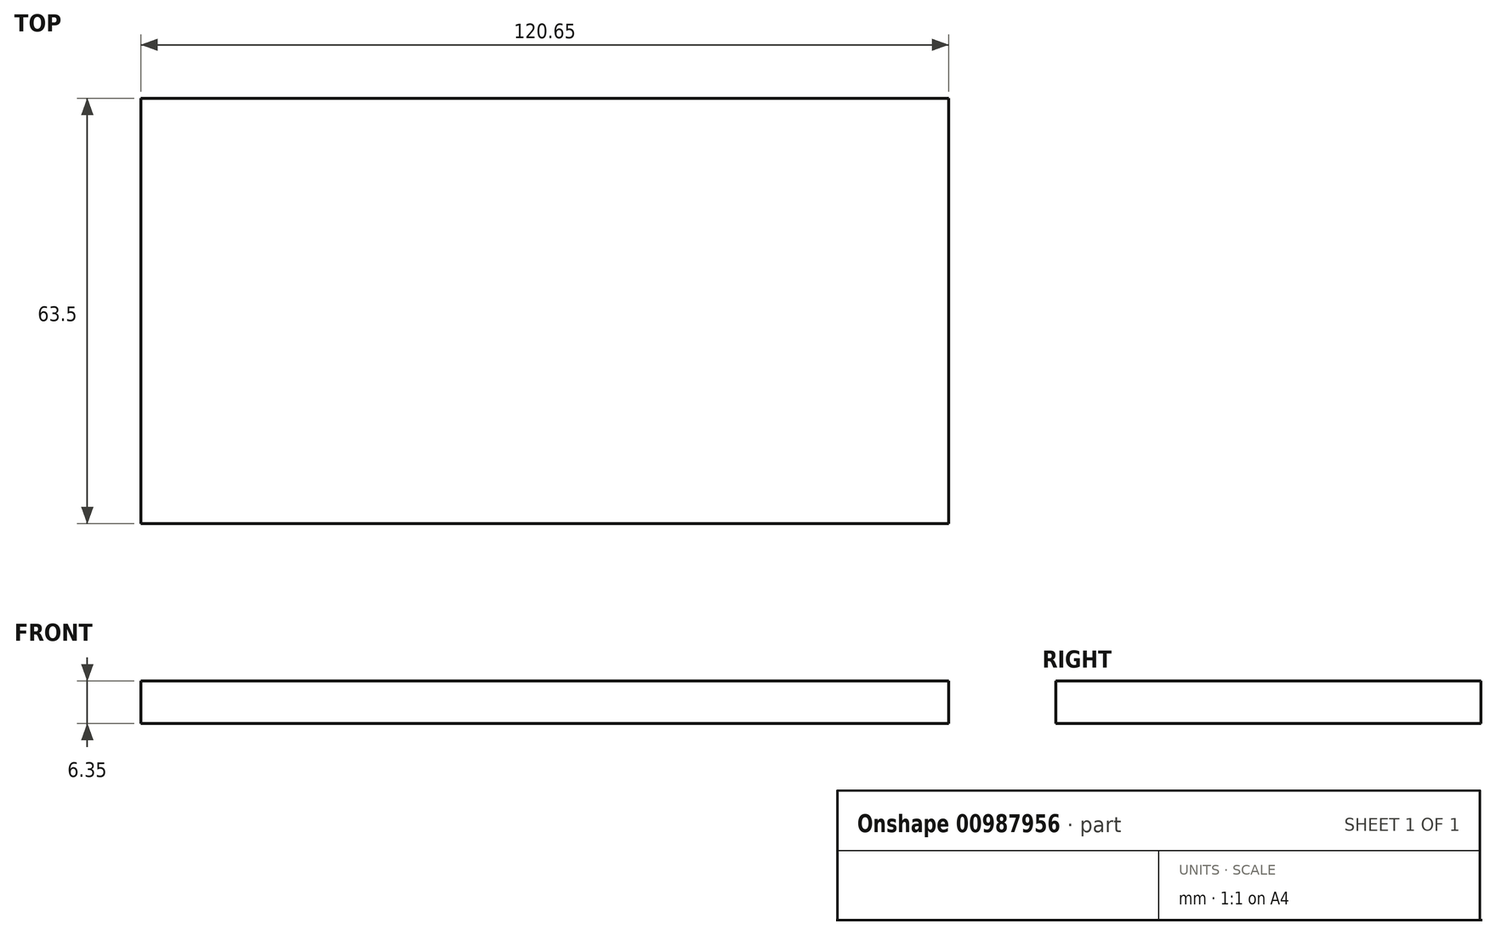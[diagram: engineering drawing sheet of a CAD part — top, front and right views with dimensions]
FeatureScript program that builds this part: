
annotation { "Feature Type Name" : "Feature", "Feature Type Description" : "" }
export const myFeature = defineFeature(function(context is Context, id is Id, definition is map)
    precondition{}
    {
        {
            var Q0;
            Q0=qCreatedBy(makeId("Top.planeOp"),FACE);
            var sketch = newSketch(context, id + "F0", { "sketchPlane" : qUnion([Q0])});
            skLineSegment(sketch, "E0.bottom", {"start": v(45.54, 49.12) * mm, "end": v(166.19, 49.12) * mm});
            skLineSegment(sketch, "E0.top", {"start": v(45.54, -14.38) * mm, "end": v(166.19, -14.38) * mm});
            skLineSegment(sketch, "E0.left", {"start": v(45.54, 49.12) * mm, "end": v(45.54, -14.38) * mm});
            skLineSegment(sketch, "E0.right", {"start": v(166.19, 49.12) * mm, "end": v(166.19, -14.38) * mm});
            skSolve(sketch);
        }
        {
            var Q0;
            Q0=makeQuery(id+"F0.imprint","IMPRINT",FACE,{"disambiguationData":[TD([[makeQuery(id+"F0.imprint","IMPRINT",EDGE,{"derivedFrom":sQuery(id+"F0.wireOp",EDGE,"E0.bottom")}),-1.0]])]});
            extrude(context, id + "F1", {"entities" : qUnion([Q0]), "depth" : 6.35 * mm, "offsetDistance" : 25.4 * mm});
        }
    });
